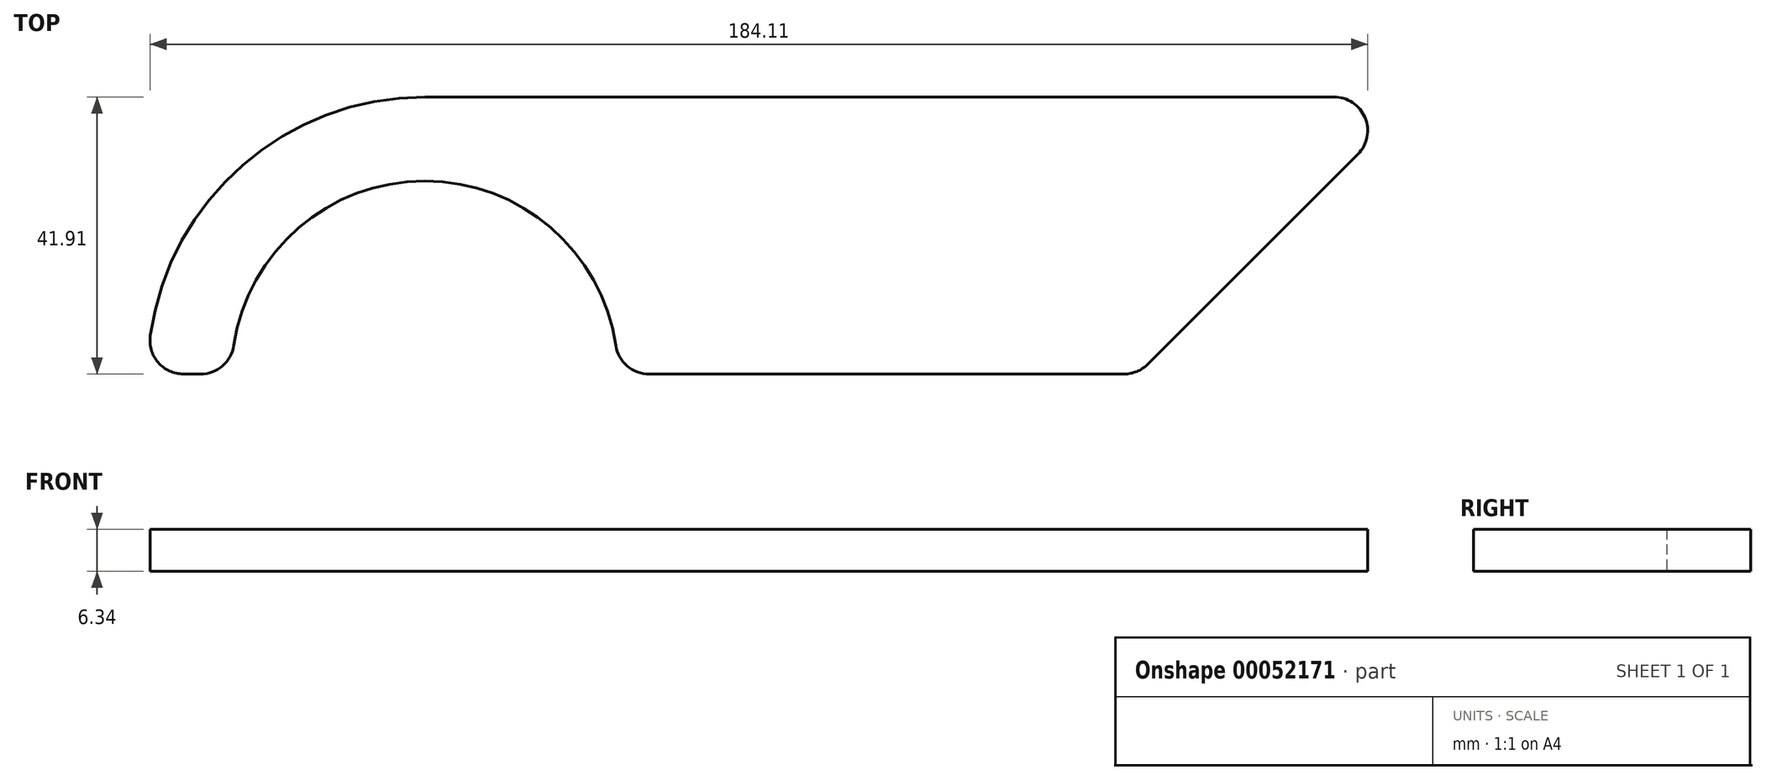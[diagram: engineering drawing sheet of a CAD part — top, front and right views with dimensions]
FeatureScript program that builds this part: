
annotation { "Feature Type Name" : "Feature", "Feature Type Description" : "" }
export const myFeature = defineFeature(function(context is Context, id is Id, definition is map)
    precondition{}
    {
        {
            var Q0;
            Q0=qCreatedBy(makeId("Top.planeOp"),FACE);
            var sketch = newSketch(context, id + "F0", { "sketchPlane" : qUnion([Q0])});
            skArc(sketch, "E0", {"start": v(29.21, 0) * mm, "mid": v(0, 29.21) * mm, "end": v(-29.21, 0) * mm});
            skArc(sketch, "E1", {"start": v(0, 41.91) * mm, "mid": v(-29.63, 29.63) * mm, "end": v(-41.91, 0) * mm});
            skLineSegment(sketch, "E2", {"start": v(-41.91, 0) * mm, "end": v(-29.21, 0) * mm});
            skLineSegment(sketch, "E3.trimOffspring", {"start": v(29.21, 0) * mm, "end": v(41.91, 0) * mm});
            skLineSegment(sketch, "E4", {"start": v(0, 0) * mm, "end": v(112.6, 112.6) * mm, "construction": true});
            skLineSegment(sketch, "E5", {"start": v(0, 41.91) * mm, "end": v(149.73, 41.91) * mm});
            skLineSegment(sketch, "E6", {"start": v(149.73, 41.91) * mm, "end": v(107.82, 0) * mm});
            skLineSegment(sketch, "E7", {"start": v(107.82, 0) * mm, "end": v(41.91, 0) * mm});
            skSolve(sketch);
        }
        {
            var Q0;
            Q0=makeQuery(id+"F0.imprint","IMPRINT",FACE,{"disambiguationData":[TD([[makeQuery(id+"F0.imprint","IMPRINT",EDGE,{"derivedFrom":sQuery(id+"F0.wireOp",EDGE,"E0")}),-1.0]])]});
            extrude(context, id + "F1", {"entities" : qUnion([Q0]), "endBound" : BoundingType.SYMMETRIC, "depth" : 6.35 * mm});
        }
        {
            var Q0;
            Q0=makeQuery(id+"F1.opExtrude","SWEPT_EDGE",EDGE,{"disambiguationData":[OSD([sQuery(id+"F0.wireOp",EDGE,"E5"),sQuery(id+"F0.wireOp",EDGE,"E6")])]});
            var Q1;
            Q1=makeQuery(id+"F1.opExtrude","SWEPT_EDGE",EDGE,{"disambiguationData":[OSD([sQuery(id+"F0.wireOp",EDGE,"E6"),sQuery(id+"F0.wireOp",EDGE,"E7")])]});
            var Q2;
            Q2=makeQuery(id+"F1.opExtrude","SWEPT_EDGE",EDGE,{"disambiguationData":[OSD([sQuery(id+"F0.wireOp",EDGE,"E0"),sQuery(id+"F0.wireOp",EDGE,"E3.trimOffspring")])]});
            var Q3;
            Q3=makeQuery(id+"F1.opExtrude","SWEPT_EDGE",EDGE,{"disambiguationData":[OSD([sQuery(id+"F0.wireOp",EDGE,"E0"),sQuery(id+"F0.wireOp",EDGE,"E2")])]});
            var Q4;
            Q4=makeQuery(id+"F1.opExtrude","SWEPT_EDGE",EDGE,{"disambiguationData":[OSD([sQuery(id+"F0.wireOp",EDGE,"E1"),sQuery(id+"F0.wireOp",EDGE,"E2")])]});
            fillet(context, id + "F2", {"entities" : qUnion([Q0, Q1, Q2, Q3, Q4]), "radius" : 5.08 * mm, "tangentPropagation" : true, "allowEdgeOverflow" : false});
        }
    });
